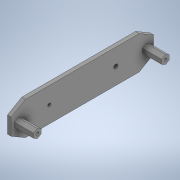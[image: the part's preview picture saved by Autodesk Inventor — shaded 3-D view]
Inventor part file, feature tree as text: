
AUTODESK INVENTOR PART (.ipt)
format: ipt  version: 2020 (Build 240168000, 168)  size: 226,304 bytes
history: native  units: in
note: dims shown in document units (in); Inventor stores cm internally (conversion verified against a paired STEP export)
features: extrude x7, sketch x7, plane x1
ambient origin geometry x8: Origin, YZ Plane, XZ Plane, XY Plane, X Axis, Y Axis, Z Axis, Center Point
bodies: Solid1 (feature_tree)
feature tree (15):
  extrude  "Extrusion1"  Depth=5.9055in
  extrude  "Extrusion3"  TaperAngle=0.0deg  [1 undecoded]
  extrude  "Extrusion4"  Depth=0.7874in
  plane  "Work Plane1"
  extrude  "Extrusion5"  Depth=0.122in
  extrude  "Extrusion6"  Depth=0.2402in
  extrude  "Extrusion7"  [1 undecoded]
  extrude  "Extrusion8"  Depth=0.0866in TaperAngle=0.0deg
  sketch  "Sketch1"  dims[d0=1.378in d1=5.9055in]
  sketch  "Sketch2"  dims[d2=0.1575in d3=0.0in]
  sketch  "Sketch3"  dims[d8=0.315in d9=0.7874in]
  sketch  "Sketch4"  dims[d10=0.0in d12=0.122in]
  sketch  "Sketch5"  dims[d13=0.0in d14=0.0in d15=0.2402in]
  sketch  "Sketch8"  dims[d16=0.0866in d17=-0.2233in]
  sketch  "Sketch9"  dims[d18=-0.3937in d19=0.0866in d20=0.0in d26=1.5748in d27=0.1654in d28=0.122in d29=1.5748in d30=0.0in d31=0.0in d32=0.2402in d33=0.0866in d34=-0.2233in]
note: 2 required parameter values undecoded (feature->parameter linkage not recoverable at this tier; creation-order binding heuristic only, values carry confidence <= 0.55)
